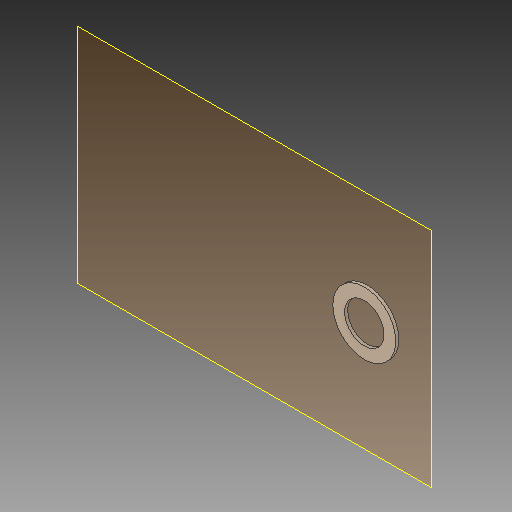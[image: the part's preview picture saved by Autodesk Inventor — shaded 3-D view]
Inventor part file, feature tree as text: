
AUTODESK INVENTOR PART (.ipt)
format: ipt  version: 2018 (Build 220112000, 112)  size: 87,552 bytes
history: native  units: mm
features: other x3, sketch x1, plane x1
ambient origin geometry x8: Origin, YZ Plane, XZ Plane, XY Plane, X Axis, Y Axis, Z Axis, Center Point
bodies: Solid1 (feature_tree)
feature tree (5):
  other  "Washer.ipt"
  other  "Solid1::Washer.ipt"
  other  "TaggingFeature1"
  sketch  "Sketch1"  dims[d0=10.0mm]
  plane  "Work Plane1"
